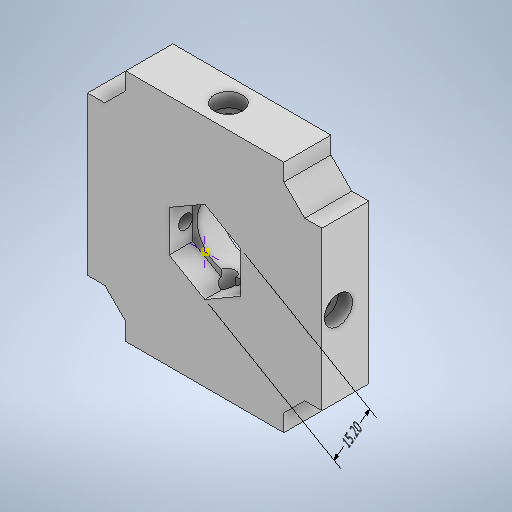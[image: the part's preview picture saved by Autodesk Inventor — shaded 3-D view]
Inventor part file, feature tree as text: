
AUTODESK INVENTOR PART (.ipt)
format: ipt  version: 2025 (Build 290162000, 162)  size: 298,496 bytes
history: native  units: mm
features: sketch x8, hole x4, extrude x2, other x1
ambient origin geometry x8: Origin, YZ Plane, XZ Plane, XY Plane, X Axis, Y Axis, Z Axis, Center Point
bodies: 实体1 (feature_tree)
feature tree (15):
  extrude  "拉伸1"  Depth=15.2mm
  sketch  "草图2"  dims[d31=5.0mm d32=0.0mm]
  sketch  "草图3"  dims[d33=13.3mm d34=6.0mm d35=4.0mm d36=2.0mm d37=90.0deg d38=0.5mm d39=20.594885mm]
  extrude  "拉伸2"  Depth=20.594885mm
  hole  "孔1"  [1 undecoded]
  hole  "孔2"  [1 undecoded]
  hole  "孔3"  [1 undecoded]
  hole  "孔4"  [1 undecoded]
  sketch  "草图1"  dims[d26=5.0mm d27=5.0mm d28=0.0mm d29=0.0mm d30=15.2mm]
  sketch  "草图4"  dims[d40=2.98mm d41=6.0mm d42=6.0mm d43=3.0mm d44=90.0deg d45=8.0mm d46=20.594885mm]
  sketch  "草图5"  dims[d47=2.98mm d48=6.0mm d49=6.0mm d50=3.0mm d51=90.0deg d52=8.0mm d53=20.594885mm]
  sketch  "草图6"  dims[d54=3.0mm d55=6.0mm d56=6.0mm d57=3.0mm d58=90.0deg d59=8.0mm d60=20.594885mm d61=15.2mm]
  sketch  "草图7"  dims[d62=5.873675mm d63=6.026246mm d64=15.2mm d65=0.25mm]
  sketch  "草图8"  dims[d66=0.375mm d67=14.3117mm d68=0.75mm d69=20.594885mm d70=0.0625mm d71=0.75mm d72=0.375mm]
  other  "线性尺寸 1"
note: 4 required parameter values undecoded (feature->parameter linkage not recoverable at this tier; creation-order binding heuristic only, values carry confidence <= 0.55)
